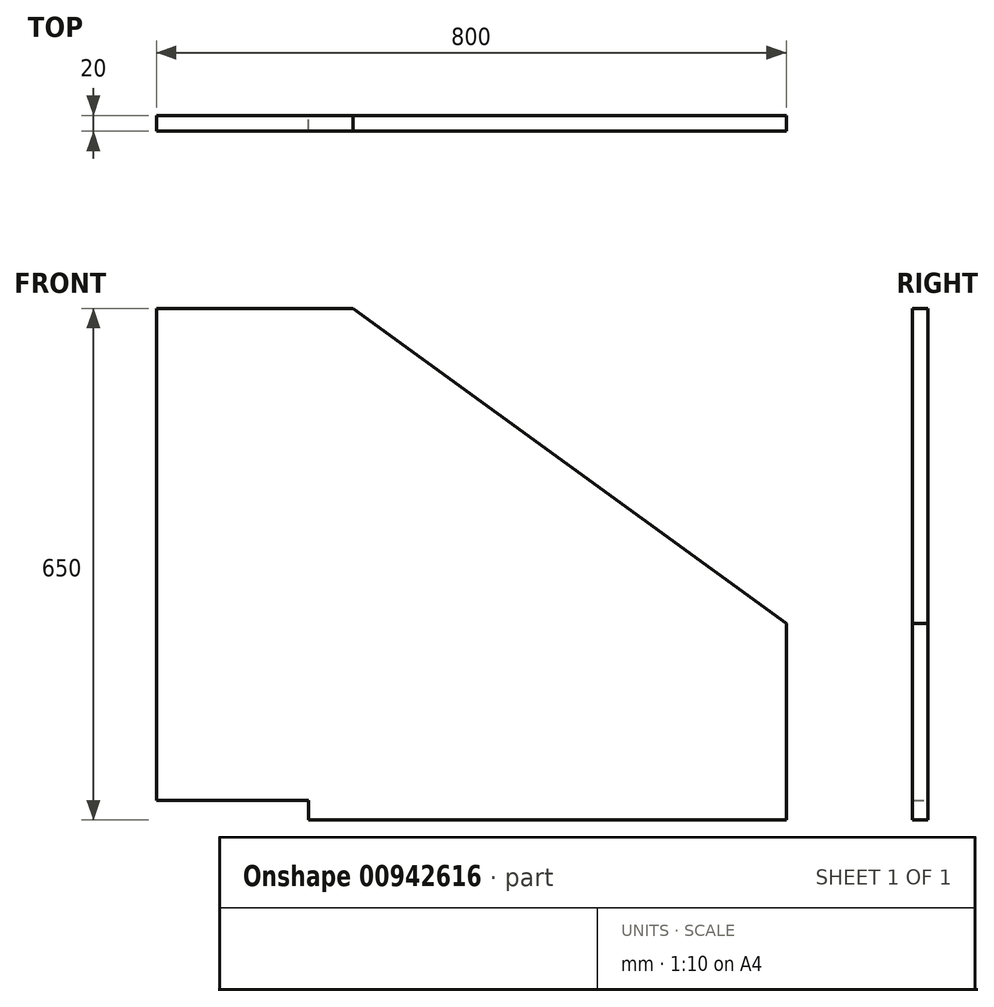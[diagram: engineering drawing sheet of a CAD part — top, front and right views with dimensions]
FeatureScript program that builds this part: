
annotation { "Feature Type Name" : "Feature", "Feature Type Description" : "" }
export const myFeature = defineFeature(function(context is Context, id is Id, definition is map)
    precondition{}
    {
        {
            var Q0;
            Q0=qCreatedBy(makeId("Front.planeOp"),FACE);
            var sketch = newSketch(context, id + "F0", { "sketchPlane" : qUnion([Q0])});
            skLineSegment(sketch, "E0.bottom", {"start": v(-400, 325) * mm, "end": v(-150, 325) * mm});
            skLineSegment(sketch, "E0.top", {"start": v(-207, -325) * mm, "end": v(400, -325) * mm});
            skLineSegment(sketch, "E0.left", {"start": v(-400, 325) * mm, "end": v(-400, -300) * mm});
            skLineSegment(sketch, "E0.right", {"start": v(400, -75) * mm, "end": v(400, -325) * mm});
            skLineSegment(sketch, "E1", {"start": v(-150, 325) * mm, "end": v(400, -75) * mm});
            skLineSegment(sketch, "E2", {"start": v(-400, -300) * mm, "end": v(-207, -300) * mm});
            skLineSegment(sketch, "E3", {"start": v(-207, -300) * mm, "end": v(-207, -325) * mm});
            skSolve(sketch);
        }
        {
            var Q0;
            Q0 = qSketchRegion(id + "F0", true);
            extrude(context, id + "F1", {"entities" : qUnion([Q0]), "depth" : 20 * mm, "offsetDistance" : 25 * mm});
        }
    });
